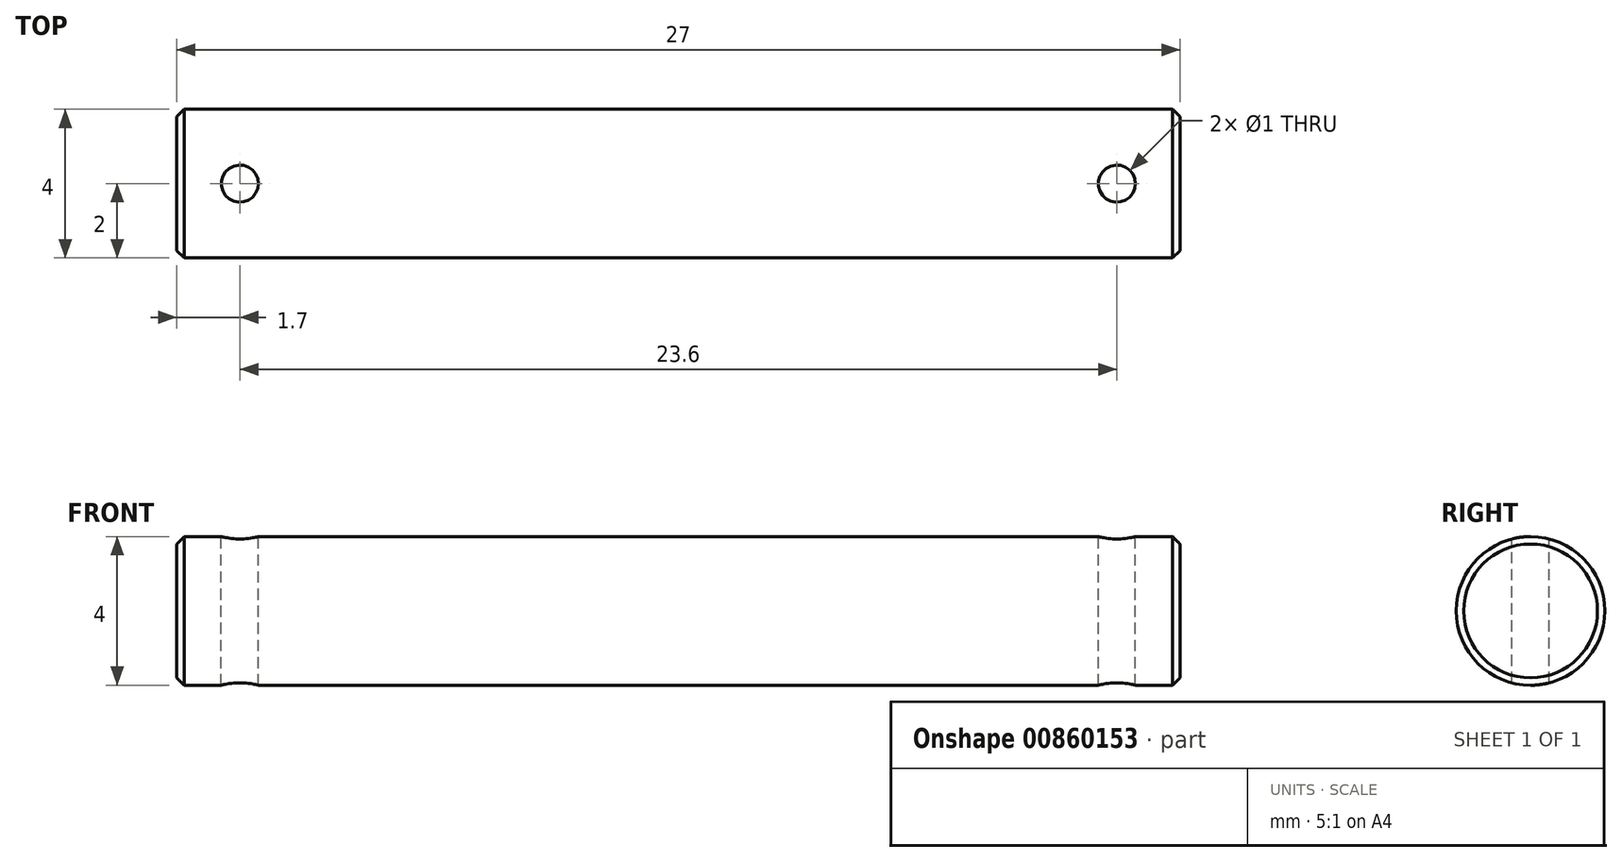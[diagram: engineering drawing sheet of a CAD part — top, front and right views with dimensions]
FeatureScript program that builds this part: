
annotation { "Feature Type Name" : "Feature", "Feature Type Description" : "" }
export const myFeature = defineFeature(function(context is Context, id is Id, definition is map)
    precondition{}
    {
        {
            var Q0;
            Q0=qCreatedBy(makeId("Front.planeOp"),FACE);
            var sketch = newSketch(context, id + "F0", { "sketchPlane" : qUnion([Q0])});
            skLineSegment(sketch, "E0", {"start": v(0, 0) * mm, "end": v(0, 2) * mm});
            skLineSegment(sketch, "E1", {"start": v(0, 2) * mm, "end": v(27, 2) * mm});
            skLineSegment(sketch, "E2", {"start": v(27, 2) * mm, "end": v(27, 0) * mm});
            skLineSegment(sketch, "E3", {"start": v(27, 0) * mm, "end": v(0, 0) * mm});
            skSolve(sketch);
        }
        {
            var Q0;
            Q0=makeQuery(id+"F0.imprint","IMPRINT",FACE,{"disambiguationData":[TD([[makeQuery(id+"F0.imprint","IMPRINT",EDGE,{"derivedFrom":sQuery(id+"F0.wireOp",EDGE,"E0")}),-1.0]])]});
            var Q1;
            Q1=sQuery(id+"F0.wireOp",EDGE,"E3");
            revolve(context, id + "F1", {"surfaceOperationType" : NewSurfaceOperationType.NEW, "entities" : qUnion([Q0]), "axis" : qUnion([Q1]), "revolveType" : RevolveType.FULL});
        }
        {
            var Q0;
            Q0=makeQuery(id+"F1.opRevolve","SWEPT_EDGE",EDGE,{"disambiguationData":[OSD([sQuery(id+"F0.wireOp",EDGE,"E0"),sQuery(id+"F0.wireOp",EDGE,"E1")])]});
            var Q1;
            Q1=makeQuery(id+"F1.opRevolve","SWEPT_EDGE",EDGE,{"disambiguationData":[OSD([sQuery(id+"F0.wireOp",EDGE,"Zi0mMb4i-wjdW-JJMa-qRUb-8dfTlUzYtq1L"),sQuery(id+"F0.wireOp",EDGE,"E2")])]});
            chamfer(context, id + "F2", {"entities" : qUnion([Q0, Q1]), "width" : 0.2 * mm, "tangentPropagation" : true});
        }
        {
            var Q0;
            Q0=qCreatedBy(makeId("Top.planeOp"),FACE);
            var sketch = newSketch(context, id + "F3", { "sketchPlane" : qUnion([Q0])});
            skCircle(sketch, "E4", {"center": v(1.7, 0) * mm, "radius": 0.5 * mm});
            skCircle(sketch, "E5", {"center": v(25.3, 0) * mm, "radius": 0.5 * mm});
            skLineSegment(sketch, "E6.0", {"start": v(0, 0) * mm, "end": v(27, 0) * mm, "construction": true});
            skLineSegment(sketch, "E7", {"start": v(13.5, 0) * mm, "end": v(13.5, 3) * mm, "construction": true});
            skSolve(sketch);
        }
        {
            var Q0;
            Q0 = qSketchRegion(id + "F3", true);
            extrude(context, id + "F4", {"entities" : qUnion([Q0]), "operationType" : NewBodyOperationType.REMOVE, "endBound" : BoundingType.SYMMETRIC, "oppositeDirection" : true, "depth" : 5 * mm, "offsetDistance" : 25 * mm});
        }
    });
